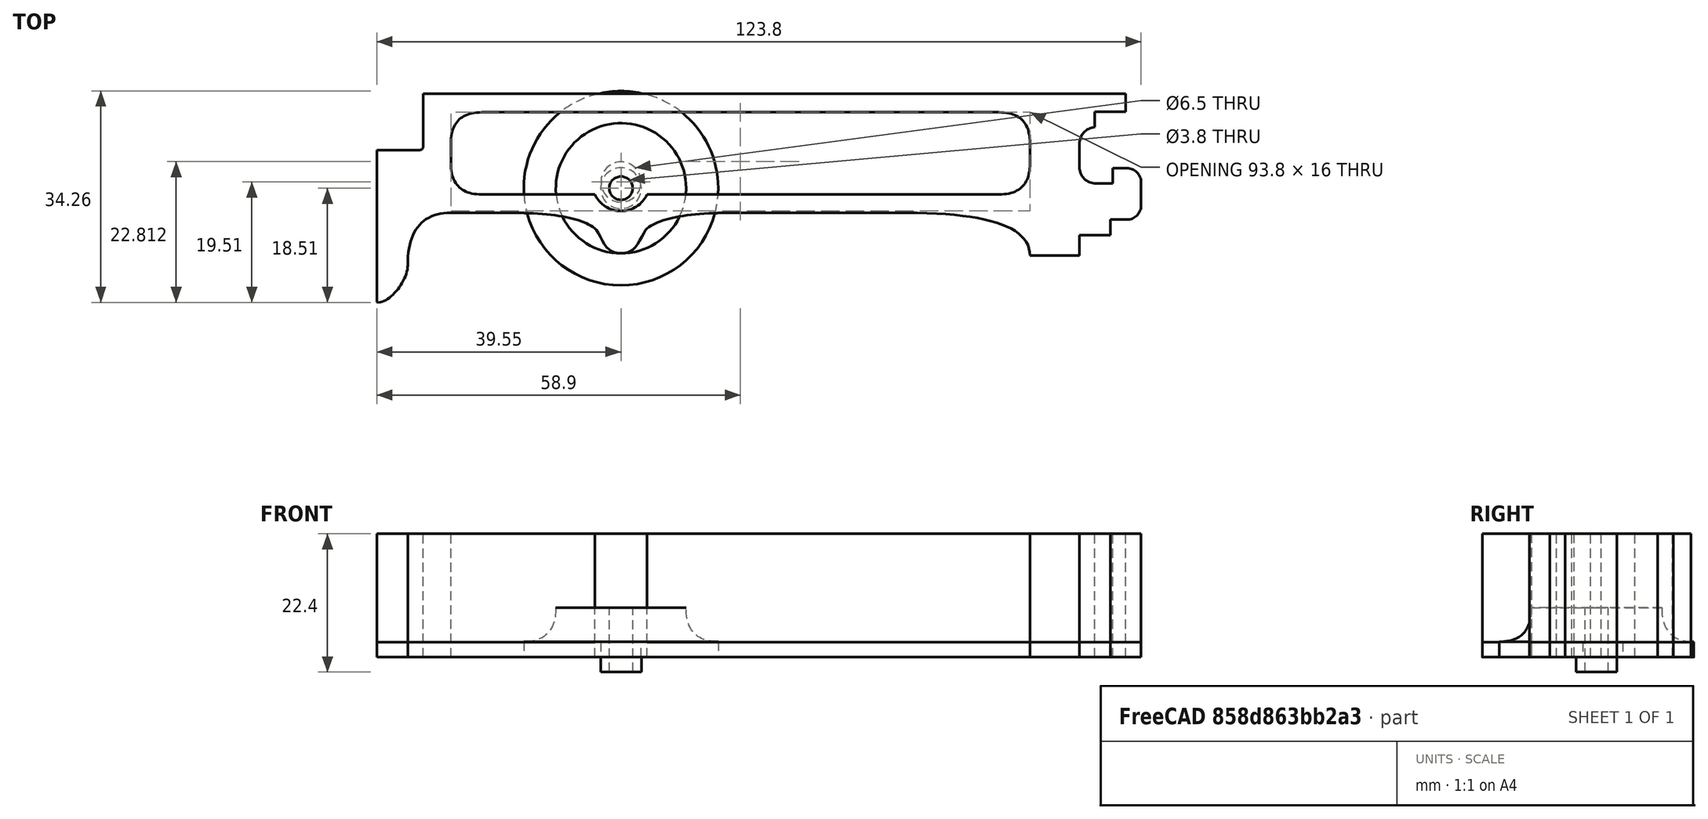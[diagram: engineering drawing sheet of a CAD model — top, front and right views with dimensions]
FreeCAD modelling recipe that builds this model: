
FCSTD DOCUMENT  (FreeCAD 0.19R0.19.2)
Label: v0_16
License: All rights reserved
LicenseURL: http://en.wikipedia.org/wiki/All_rights_reserved
objects: Sketcher::SketchObject×3, Part::Extrusion×2, Part::Revolution×1
note: 6 computed .brp shape members not serialized (recipe doc carries the construction recipe); baked Part::Feature solids carry a one-line shape summary decoded from their .brp

FEATURE [Sketcher::SketchObject] Sketch
  FullyConstrained = true
  sketch-geometry (69):
    g0: ArcOfCircle CenterX=-20 CenterY=-14.35 CenterZ=0 NormalX=0 NormalY=0 NormalZ=1 AngleXU=0 Radius=2.3 StartAngle=8e-16 EndAngle=1.5708
    g1: ArcOfCircle CenterX=-20 CenterY=-18.1 CenterZ=0 NormalX=0 NormalY=0 NormalZ=1 AngleXU=0 Radius=2.3 StartAngle=4.71239 EndAngle=6.28319
    g2: LineSegment StartX=-20 StartY=-20.4 StartZ=0 EndX=-22.7 EndY=-20.4 EndZ=0
    g3: LineSegment StartX=-22.7 StartY=-22.9 StartZ=0 EndX=-22.7 EndY=-20.4 EndZ=0
    g4: LineSegment StartX=-17.7 StartY=-14.35 StartZ=0 EndX=-17.7 EndY=-18.1 EndZ=0
    g5: LineSegment StartX=-25.2 StartY=-5.40742 StartZ=0 EndX=-25.2 EndY=-2.9 EndZ=0
    g6: LineSegment StartX=-25.2 StartY=-2.9 StartZ=0 EndX=-20.2 EndY=-2.9 EndZ=0
    g7: LineSegment StartX=-20.2 StartY=-2.9 StartZ=0 EndX=-20.2 EndY=0 EndZ=0
    g8: ArcOfCircle CenterX=-25 CenterY=-8.1 CenterZ=0 NormalX=0 NormalY=0 NormalZ=1 AngleXU=0 Radius=2.7 StartAngle=1.64494 EndAngle=3.14159
    g9: ArcOfCircle CenterX=-25 CenterY=-11.85 CenterZ=0 NormalX=0 NormalY=0 NormalZ=1 AngleXU=0 Radius=2.7 StartAngle=3.14159 EndAngle=4.71239
    g10: LineSegment StartX=-27.7 StartY=-8.1 StartZ=0 EndX=-27.7 EndY=-11.85 EndZ=0
    g11: LineSegment StartX=-25 StartY=-14.55 StartZ=0 EndX=-22.3 EndY=-14.55 EndZ=0
    g12: LineSegment StartX=-22.3 StartY=-12.05 StartZ=0 EndX=-22.3 EndY=-14.55 EndZ=0
    g13: LineSegment StartX=-22.3 StartY=-12.05 StartZ=0 EndX=-20 EndY=-12.05 EndZ=0
    g14: LineSegment StartX=-27.7 StartY=-22.9 StartZ=0 EndX=-22.7 EndY=-22.9 EndZ=0
    g15: LineSegment StartX=-27.7 StartY=-22.9 StartZ=0 EndX=-27.7 EndY=-26.2 EndZ=0
    g16: Circle CenterX=-101.95 CenterY=-14.3 CenterZ=0 NormalX=0 NormalY=0 NormalZ=1 AngleXU=0 Radius=3.25
    g17: LineSegment StartX=-134 StartY=0 StartZ=0 EndX=-20.2 EndY=0 EndZ=0
    g18: LineSegment StartX=-134 StartY=2.68e-14 StartZ=0 EndX=-134 EndY=-8.6 EndZ=0
    g19: LineSegment StartX=-134.5 StartY=-9.1 StartZ=0 EndX=-141.5 EndY=-9.1 EndZ=0
    g20: ArcOfCircle CenterX=-134.5 CenterY=-8.6 CenterZ=0 NormalX=0 NormalY=0 NormalZ=1 AngleXU=0 Radius=0.5 StartAngle=4.71239 EndAngle=6.28319
    g21: Circle CenterX=-97.7 CenterY=-21.8 CenterZ=0 NormalX=0 NormalY=0 NormalZ=1 AngleXU=0 Radius=1
    g22: Circle CenterX=-94.45 CenterY=-19.3 CenterZ=0 NormalX=0 NormalY=0 NormalZ=1 AngleXU=0 Radius=1
    g23: Circle CenterX=-84.45 CenterY=-19.3 CenterZ=0 NormalX=0 NormalY=0 NormalZ=1 AngleXU=0 Radius=1
    g24: BSplineCurve PolesCount=3 KnotsCount=2 Degree=2 IsPeriodic=0
    g25: GeomPoint X=-97.7 Y=-21.8 Z=0
    g26: GeomPoint X=-84.45 Y=-19.3 Z=0
    g27: Circle CenterX=-106.2 CenterY=-21.8 CenterZ=0 NormalX=0 NormalY=0 NormalZ=1 AngleXU=0 Radius=1
    g28: Circle CenterX=-109.45 CenterY=-19.3 CenterZ=0 NormalX=0 NormalY=0 NormalZ=1 AngleXU=0 Radius=1
    g29: Circle CenterX=-119.45 CenterY=-19.3 CenterZ=0 NormalX=0 NormalY=0 NormalZ=1 AngleXU=0 Radius=1
    g30: BSplineCurve PolesCount=3 KnotsCount=2 Degree=2 IsPeriodic=0
    g31: GeomPoint X=-106.2 Y=-21.8 Z=0
    g32: GeomPoint X=-119.45 Y=-19.3 Z=0
    g33: LineSegment StartX=-141.5 StartY=-9.1 StartZ=0 EndX=-141.5 EndY=-33.8 EndZ=0
    g34-g37: Circle x4 (B-spline internal-alignment scaffolding for g38; pole/knot coordinates omitted)
    g38: BSplineCurve PolesCount=4 KnotsCount=2 Degree=3 IsPeriodic=0
    g39: GeomPoint X=-141.5 Y=-33.8 Z=0
    g40: GeomPoint X=-136.5 Y=-27.8 Z=0
    g41: Circle CenterX=-136.5 CenterY=-27.8 CenterZ=0 NormalX=0 NormalY=0 NormalZ=1 AngleXU=0 Radius=1
    g42: Circle CenterX=-136.5 CenterY=-19.3 CenterZ=0 NormalX=0 NormalY=0 NormalZ=1 AngleXU=0 Radius=1
    g43: Circle CenterX=-129.5 CenterY=-19.3 CenterZ=0 NormalX=0 NormalY=0 NormalZ=1 AngleXU=0 Radius=1
    g44: BSplineCurve PolesCount=3 KnotsCount=2 Degree=2 IsPeriodic=0
    g45: GeomPoint X=-136.5 Y=-27.8 Z=0
    g46: GeomPoint X=-129.5 Y=-19.3 Z=0
    g47: LineSegment StartX=-129.5 StartY=-19.3 StartZ=0 EndX=-119.45 EndY=-19.3 EndZ=0
    g48: LineSegment StartX=-35.7 StartY=-26.2 StartZ=0 EndX=-27.7 EndY=-26.2 EndZ=0
    g49: Circle CenterX=-35.7 CenterY=-26.2 CenterZ=0 NormalX=0 NormalY=0 NormalZ=1 AngleXU=0 Radius=1
    g50: Circle CenterX=-35.7 CenterY=-19.3 CenterZ=0 NormalX=0 NormalY=0 NormalZ=1 AngleXU=0 Radius=1
    g51: Circle CenterX=-55.7 CenterY=-19.3 CenterZ=0 NormalX=0 NormalY=0 NormalZ=1 AngleXU=0 Radius=1
    g52: BSplineCurve PolesCount=3 KnotsCount=2 Degree=2 IsPeriodic=0
    g53: GeomPoint X=-35.7 Y=-26.2 Z=0
    g54: GeomPoint X=-55.7 Y=-19.3 Z=0
    g55: LineSegment StartX=-84.45 StartY=-19.3 StartZ=0 EndX=-55.7 EndY=-19.3 EndZ=0
    g56-g62: Circle x7 (B-spline internal-alignment scaffolding for g63; pole/knot coordinates omitted)
    g63: BSplineCurve PolesCount=7 KnotsCount=5 Degree=3 IsPeriodic=0
    g64-g68: GeomPoint x5 (B-spline internal-alignment scaffolding for g63; pole/knot coordinates omitted)
  constraints (111):
    c: Block(g1)
    c: Block(g0)
    c: Coincident(g2,g1)
    c: Horizontal(g2)
    c: Vertical(g3)
    c: Coincident(g3,g2)
    c: Coincident(g4,g0)
    c: Coincident(g4,g1)
    c: Vertical(g4)
    c: Vertical(g5)
    c: Block(g5)
    c: Coincident(g6,g5)
    c: Horizontal(g6)
    c: Vertical(g7)
    c: Block(g7)
    c: Block(g6)
    c: Coincident(g8,g5)
    c: Block(g9)
    c: Coincident(g10,g8)
    c: Coincident(g10,g9)
    c: Vertical(g10)
    c: Block(g10)
    c: Coincident(g11,g9)
    c: Horizontal(g11)
    c: Vertical(g12)
    c: Coincident(g12,g11)
    c: Block(g12)
    c: Coincident(g13,g0)
    c: Horizontal(g13)
    c: Block(g13)
    c: Coincident(g14,g3)
    c: Horizontal(g14)
    c: Block(g14)
    c: Coincident(g15,g14)
    c: Vertical(g15)
    c: Block(g16)
    c: Coincident(g17,g7)
    c: Horizontal(g17)
    c: Vertical(g18)
    c: Distance(g18) = 8.6
    c: Horizontal(g19)
    c: Distance(g19) = 7
    c: Coincident(g20,g18)
    c: Coincident(g20,g19)
    c: Block(g20)
    c: Block(g17)
    c: Weight(g21) = 1
    c: Equal(g21,g22)
    c: Equal(g21,g23)
    c: InternalAlignment(g21,g24)
    c: InternalAlignment(g22,g24)
    c: InternalAlignment(g23,g24)
    c: InternalAlignment(g25,g24)
    c: InternalAlignment(g26,g24)
    c: Weight(g27) = 1
    c: Equal(g27,g28)
    c: Equal(g27,g29)
    c: InternalAlignment(g27,g30)
    c: InternalAlignment(g28,g30)
    c: InternalAlignment(g29,g30)
    c: InternalAlignment(g31,g30)
    c: InternalAlignment(g32,g30)
    c: Block(g30)
    c: Block(g24)
    c: Coincident(g33,g19)
    c: Vertical(g33)
    c: Block(g33)
    c: Coincident(g38,g33)
    c: Weight(g34) = 1
    c: Equal(g34,g35)
    c: Equal(g34,g36)
    c: Equal(g34,g37)
    c: InternalAlignment(g34-g37 -> g38) x4
    c: InternalAlignment(g39,g38)
    c: InternalAlignment(g40,g38)
    c: Weight(g41) = 1
    c: Equal(g41,g42)
    c: Equal(g41,g43)
    c: InternalAlignment(g41,g44)
    c: InternalAlignment(g42,g44)
    c: InternalAlignment(g43,g44)
    c: InternalAlignment(g45,g44)
    c: InternalAlignment(g46,g44)
    c: Block(g38)
    c: Block(g44)
    c: Coincident(g47,g44)
    c: Coincident(g47,g30)
    c: Horizontal(g47)
    c: Horizontal(g48)
    c: Distance(g48) = 8
    c: Block(g48)
    c: Block(g15)
    c: Block(g8)
    c: Coincident(g52,g48)
    c: Weight(g49) = 1
    c: Equal(g49,g50)
    c: Equal(g49,g51)
    c: InternalAlignment(g49,g52)
    c: InternalAlignment(g50,g52)
    c: InternalAlignment(g51,g52)
    c: InternalAlignment(g53,g52)
    c: InternalAlignment(g54,g52)
    c: Block(g52)
    c: Coincident(g55,g24)
    c: Coincident(g55,g52)
    c: Horizontal(g55)
    c: Weight(g56) = 1
    c: Equal(g56, g57-g62) x6
    c: InternalAlignment(g56-g62 -> g63) x7
    c: InternalAlignment(g64-g68 -> g63) x5
    c: Block(g63)
FEATURE [Part::Extrusion] Extrude
  Base = -> Sketch
  Dir = (0,0,1)
  DirMode = 2
  FaceMakerClass = Part::FaceMakerBullseye
  LengthFwd = 2.4
  LengthRev = 0
  Solid = true
  Symmetric = false
FEATURE [Sketcher::SketchObject] Sketch001
  FullyConstrained = true
  sketch-geometry (98):
    g0: ArcOfCircle CenterX=-20 CenterY=-14.35 CenterZ=0 NormalX=0 NormalY=0 NormalZ=1 AngleXU=0 Radius=2.3 StartAngle=8e-16 EndAngle=1.5708
    g1: ArcOfCircle CenterX=-20 CenterY=-18.1 CenterZ=0 NormalX=0 NormalY=0 NormalZ=1 AngleXU=0 Radius=2.3 StartAngle=4.71239 EndAngle=6.28319
    g2: LineSegment StartX=-20 StartY=-20.4 StartZ=0 EndX=-22.7 EndY=-20.4 EndZ=0
    g3: LineSegment StartX=-22.7 StartY=-22.9 StartZ=0 EndX=-22.7 EndY=-20.4 EndZ=0
    g4: LineSegment StartX=-17.7 StartY=-14.35 StartZ=0 EndX=-17.7 EndY=-18.1 EndZ=0
    g5: LineSegment StartX=-25.2 StartY=-5.40742 StartZ=0 EndX=-25.2 EndY=-2.9 EndZ=0
    g6: LineSegment StartX=-25.2 StartY=-2.9 StartZ=0 EndX=-20.2 EndY=-2.9 EndZ=0
    g7: LineSegment StartX=-20.2 StartY=-2.9 StartZ=0 EndX=-20.2 EndY=0 EndZ=0
    g8: ArcOfCircle CenterX=-25 CenterY=-8.1 CenterZ=0 NormalX=0 NormalY=0 NormalZ=1 AngleXU=0 Radius=2.7 StartAngle=1.64494 EndAngle=3.14159
    g9: ArcOfCircle CenterX=-25 CenterY=-11.85 CenterZ=0 NormalX=0 NormalY=0 NormalZ=1 AngleXU=0 Radius=2.7 StartAngle=3.14159 EndAngle=4.71239
    g10: LineSegment StartX=-27.7 StartY=-8.1 StartZ=0 EndX=-27.7 EndY=-11.85 EndZ=0
    g11: LineSegment StartX=-25 StartY=-14.55 StartZ=0 EndX=-22.3 EndY=-14.55 EndZ=0
    g12: LineSegment StartX=-22.3 StartY=-12.05 StartZ=0 EndX=-22.3 EndY=-14.55 EndZ=0
    g13: LineSegment StartX=-22.3 StartY=-12.05 StartZ=0 EndX=-20 EndY=-12.05 EndZ=0
    g14: LineSegment StartX=-27.7 StartY=-22.9 StartZ=0 EndX=-22.7 EndY=-22.9 EndZ=0
    g15: LineSegment StartX=-27.7 StartY=-22.9 StartZ=0 EndX=-27.7 EndY=-26.2 EndZ=0
    g16: LineSegment StartX=-134 StartY=0 StartZ=0 EndX=-134 EndY=-8.6 EndZ=0
    g17: LineSegment StartX=-134.5 StartY=-9.1 StartZ=0 EndX=-141.5 EndY=-9.1 EndZ=0
    g18: ArcOfCircle CenterX=-134.5 CenterY=-8.6 CenterZ=0 NormalX=0 NormalY=0 NormalZ=1 AngleXU=0 Radius=0.5 StartAngle=4.71239 EndAngle=6.28319
    g19: Circle CenterX=-97.7 CenterY=-21.8 CenterZ=0 NormalX=0 NormalY=0 NormalZ=1 AngleXU=0 Radius=1
    g20: Circle CenterX=-94.45 CenterY=-19.3 CenterZ=0 NormalX=0 NormalY=0 NormalZ=1 AngleXU=0 Radius=1
    g21: Circle CenterX=-84.45 CenterY=-19.3 CenterZ=0 NormalX=0 NormalY=0 NormalZ=1 AngleXU=0 Radius=1
    g22: BSplineCurve PolesCount=3 KnotsCount=2 Degree=2 IsPeriodic=0
    g23: GeomPoint X=-97.7 Y=-21.8 Z=0
    g24: GeomPoint X=-84.45 Y=-19.3 Z=0
    g25: Circle CenterX=-106.2 CenterY=-21.8 CenterZ=0 NormalX=0 NormalY=0 NormalZ=1 AngleXU=0 Radius=1
    g26: Circle CenterX=-109.45 CenterY=-19.3 CenterZ=0 NormalX=0 NormalY=0 NormalZ=1 AngleXU=0 Radius=1
    g27: Circle CenterX=-119.45 CenterY=-19.3 CenterZ=0 NormalX=0 NormalY=0 NormalZ=1 AngleXU=0 Radius=1
    g28: BSplineCurve PolesCount=3 KnotsCount=2 Degree=2 IsPeriodic=0
    g29: GeomPoint X=-106.2 Y=-21.8 Z=0
    g30: GeomPoint X=-119.45 Y=-19.3 Z=0
    g31: LineSegment StartX=-141.5 StartY=-9.1 StartZ=0 EndX=-141.5 EndY=-33.8 EndZ=0
    g32-g35: Circle x4 (B-spline internal-alignment scaffolding for g36; pole/knot coordinates omitted)
    g36: BSplineCurve PolesCount=4 KnotsCount=2 Degree=3 IsPeriodic=0
    g37: GeomPoint X=-141.5 Y=-33.8 Z=0
    g38: GeomPoint X=-136.5 Y=-27.8 Z=0
    g39: Circle CenterX=-136.5 CenterY=-27.8 CenterZ=0 NormalX=0 NormalY=0 NormalZ=1 AngleXU=0 Radius=1
    g40: Circle CenterX=-136.5 CenterY=-19.3 CenterZ=0 NormalX=0 NormalY=0 NormalZ=1 AngleXU=0 Radius=1
    g41: Circle CenterX=-129.5 CenterY=-19.3 CenterZ=0 NormalX=0 NormalY=0 NormalZ=1 AngleXU=0 Radius=1
    g42: BSplineCurve PolesCount=3 KnotsCount=2 Degree=2 IsPeriodic=0
    g43: GeomPoint X=-136.5 Y=-27.8 Z=0
    g44: GeomPoint X=-129.5 Y=-19.3 Z=0
    g45: LineSegment StartX=-129.5 StartY=-19.3 StartZ=0 EndX=-119.45 EndY=-19.3 EndZ=0
    g46: LineSegment StartX=-35.7 StartY=-26.2 StartZ=0 EndX=-27.7 EndY=-26.2 EndZ=0
    g47: Circle CenterX=-35.7 CenterY=-26.2 CenterZ=0 NormalX=0 NormalY=0 NormalZ=1 AngleXU=0 Radius=1
    g48: Circle CenterX=-35.7 CenterY=-19.3 CenterZ=0 NormalX=0 NormalY=0 NormalZ=1 AngleXU=0 Radius=1
    g49: Circle CenterX=-55.7 CenterY=-19.3 CenterZ=0 NormalX=0 NormalY=0 NormalZ=1 AngleXU=0 Radius=1
    g50: BSplineCurve PolesCount=3 KnotsCount=2 Degree=2 IsPeriodic=0
    g51: GeomPoint X=-35.7 Y=-26.2 Z=0
    g52: GeomPoint X=-55.7 Y=-19.3 Z=0
    g53: LineSegment StartX=-84.45 StartY=-19.3 StartZ=0 EndX=-55.7 EndY=-19.3 EndZ=0
    g54-g60: Circle x7 (B-spline internal-alignment scaffolding for g61; pole/knot coordinates omitted)
    g61: BSplineCurve PolesCount=7 KnotsCount=5 Degree=3 IsPeriodic=0
    g62-g66: GeomPoint x5 (B-spline internal-alignment scaffolding for g61; pole/knot coordinates omitted)
    g67: LineSegment StartX=-134 StartY=0 StartZ=0 EndX=-20.2 EndY=0 EndZ=0
    g68: ArcOfCircle CenterX=-101.95 CenterY=-14.3 CenterZ=0 NormalX=0 NormalY=0 NormalZ=1 AngleXU=0 Radius=4.69707 StartAngle=3.58144 EndAngle=5.84334
    g69: Circle CenterX=-40.7 CenterY=-3 CenterZ=0 NormalX=0 NormalY=0 NormalZ=1 AngleXU=0 Radius=1
    g70: Circle CenterX=-35.7 CenterY=-3 CenterZ=0 NormalX=0 NormalY=0 NormalZ=1 AngleXU=0 Radius=1
    g71: Circle CenterX=-35.7 CenterY=-8 CenterZ=0 NormalX=0 NormalY=0 NormalZ=1 AngleXU=0 Radius=1
    g72: BSplineCurve PolesCount=3 KnotsCount=2 Degree=2 IsPeriodic=0
    g73: GeomPoint X=-40.7 Y=-3 Z=0
    g74: GeomPoint X=-35.7 Y=-8 Z=0
    g75: Circle CenterX=-35.7 CenterY=-11.3 CenterZ=0 NormalX=0 NormalY=0 NormalZ=1 AngleXU=0 Radius=1
    g76: Circle CenterX=-35.7 CenterY=-16.3 CenterZ=0 NormalX=0 NormalY=0 NormalZ=1 AngleXU=0 Radius=1
    g77: Circle CenterX=-40.7 CenterY=-16.3 CenterZ=0 NormalX=0 NormalY=0 NormalZ=1 AngleXU=0 Radius=1
    g78: BSplineCurve PolesCount=3 KnotsCount=2 Degree=2 IsPeriodic=0
    g79: GeomPoint X=-35.7 Y=-11.3 Z=0
    g80: GeomPoint X=-40.7 Y=-16.3 Z=0
    g81: Circle CenterX=-124.5 CenterY=-16.3 CenterZ=0 NormalX=0 NormalY=0 NormalZ=1 AngleXU=0 Radius=1
    g82: Circle CenterX=-129.5 CenterY=-16.3 CenterZ=0 NormalX=0 NormalY=0 NormalZ=1 AngleXU=0 Radius=1
    g83: Circle CenterX=-129.5 CenterY=-11.3 CenterZ=0 NormalX=0 NormalY=0 NormalZ=1 AngleXU=0 Radius=1
    g84: BSplineCurve PolesCount=3 KnotsCount=2 Degree=2 IsPeriodic=0
    g85: GeomPoint X=-124.5 Y=-16.3 Z=0
    g86: GeomPoint X=-129.5 Y=-11.3 Z=0
    g87: Circle CenterX=-129.5 CenterY=-8 CenterZ=0 NormalX=0 NormalY=0 NormalZ=1 AngleXU=0 Radius=1
    g88: Circle CenterX=-129.5 CenterY=-3 CenterZ=0 NormalX=0 NormalY=0 NormalZ=1 AngleXU=0 Radius=1
    g89: Circle CenterX=-124.5 CenterY=-3 CenterZ=0 NormalX=0 NormalY=0 NormalZ=1 AngleXU=0 Radius=1
    g90: BSplineCurve PolesCount=3 KnotsCount=2 Degree=2 IsPeriodic=0
    g91: GeomPoint X=-129.5 Y=-8 Z=0
    g92: GeomPoint X=-124.5 Y=-3 Z=0
    g93: LineSegment StartX=-129.5 StartY=-8 StartZ=0 EndX=-129.5 EndY=-11.3 EndZ=0
    g94: LineSegment StartX=-124.5 StartY=-3 StartZ=0 EndX=-40.7 EndY=-3 EndZ=0
    g95: LineSegment StartX=-35.7 StartY=-8 StartZ=0 EndX=-35.7 EndY=-11.3 EndZ=0
    g96: LineSegment StartX=-40.7 StartY=-16.3 StartZ=0 EndX=-97.7 EndY=-16.3 EndZ=0
    g97: LineSegment StartX=-106.2 StartY=-16.3 StartZ=0 EndX=-124.5 EndY=-16.3 EndZ=0
  constraints (162):
    c: Block(g1)
    c: Block(g0)
    c: Coincident(g2,g1)
    c: Horizontal(g2)
    c: Vertical(g3)
    c: Coincident(g3,g2)
    c: Coincident(g4,g0)
    c: Coincident(g4,g1)
    c: Vertical(g4)
    c: Vertical(g5)
    c: Block(g5)
    c: Coincident(g6,g5)
    c: Horizontal(g6)
    c: Vertical(g7)
    c: Block(g7)
    c: Block(g6)
    c: Coincident(g8,g5)
    c: Block(g9)
    c: Coincident(g10,g8)
    c: Coincident(g10,g9)
    c: Vertical(g10)
    c: Block(g10)
    c: Coincident(g11,g9)
    c: Horizontal(g11)
    c: Vertical(g12)
    c: Coincident(g12,g11)
    c: Block(g12)
    c: Coincident(g13,g0)
    c: Horizontal(g13)
    c: Block(g13)
    c: Coincident(g14,g3)
    c: Horizontal(g14)
    c: Block(g14)
    c: Coincident(g15,g14)
    c: Vertical(g15)
    c: Vertical(g16)
    c: Distance(g16) = 8.6
    c: Horizontal(g17)
    c: Distance(g17) = 7
    c: Coincident(g18,g16)
    c: Coincident(g18,g17)
    c: Block(g18)
    c: Weight(g19) = 1
    c: Equal(g19,g20)
    c: Equal(g19,g21)
    c: InternalAlignment(g19,g22)
    c: InternalAlignment(g20,g22)
    c: InternalAlignment(g21,g22)
    c: InternalAlignment(g23,g22)
    c: InternalAlignment(g24,g22)
    c: Weight(g25) = 1
    c: Equal(g25,g26)
    c: Equal(g25,g27)
    c: InternalAlignment(g25,g28)
    c: InternalAlignment(g26,g28)
    c: InternalAlignment(g27,g28)
    c: InternalAlignment(g29,g28)
    c: InternalAlignment(g30,g28)
    c: Block(g22)
    c: Coincident(g31,g17)
    c: Vertical(g31)
    c: Block(g31)
    c: Coincident(g36,g31)
    c: Weight(g32) = 1
    c: Equal(g32,g33)
    c: Equal(g32,g34)
    c: Equal(g32,g35)
    c: InternalAlignment(g32-g35 -> g36) x4
    c: InternalAlignment(g37,g36)
    c: InternalAlignment(g38,g36)
    c: Weight(g39) = 1
    c: Equal(g39,g40)
    c: Equal(g39,g41)
    c: InternalAlignment(g39,g42)
    c: InternalAlignment(g40,g42)
    c: InternalAlignment(g41,g42)
    c: InternalAlignment(g43,g42)
    c: InternalAlignment(g44,g42)
    c: Block(g36)
    c: Coincident(g45,g42)
    c: Coincident(g45,g28)
    c: Horizontal(g45)
    c: Horizontal(g46)
    c: Distance(g46) = 8
    c: Block(g46)
    c: Block(g15)
    c: Block(g8)
    c: Coincident(g50,g46)
    c: Weight(g47) = 1
    c: Equal(g47,g48)
    c: Equal(g47,g49)
    c: InternalAlignment(g47,g50)
    c: InternalAlignment(g48,g50)
    c: InternalAlignment(g49,g50)
    c: InternalAlignment(g51,g50)
    c: InternalAlignment(g52,g50)
    c: Block(g50)
    c: Coincident(g53,g22)
    c: Coincident(g53,g50)
    c: Horizontal(g53)
    c: Weight(g54) = 1
    c: Equal(g54, g55-g60) x6
    c: InternalAlignment(g54-g60 -> g61) x7
    c: InternalAlignment(g62-g66 -> g61) x5
    c: Block(g61)
    c: Coincident(g67,g16)
    c: Coincident(g67,g7)
    c: Horizontal(g67)
    c: Block(g68)
    c: Block(g28)
    c: Block(g42)
    c: Weight(g69) = 1
    c: Equal(g69,g70)
    c: Equal(g69,g71)
    c: InternalAlignment(g69,g72)
    c: InternalAlignment(g70,g72)
    c: InternalAlignment(g71,g72)
    c: InternalAlignment(g73,g72)
    c: InternalAlignment(g74,g72)
    c: Weight(g75) = 1
    c: Equal(g75,g76)
    c: Equal(g75,g77)
    c: InternalAlignment(g75,g78)
    c: InternalAlignment(g76,g78)
    c: InternalAlignment(g77,g78)
    c: InternalAlignment(g79,g78)
    c: InternalAlignment(g80,g78)
    c: Weight(g81) = 1
    c: Equal(g81,g82)
    c: Equal(g81,g83)
    c: InternalAlignment(g81,g84)
    c: InternalAlignment(g82,g84)
    c: InternalAlignment(g83,g84)
    c: InternalAlignment(g85,g84)
    c: InternalAlignment(g86,g84)
    c: Weight(g87) = 1
    c: Equal(g87,g88)
    c: Equal(g87,g89)
    c: InternalAlignment(g87,g90)
    c: InternalAlignment(g88,g90)
    c: InternalAlignment(g89,g90)
    c: InternalAlignment(g91,g90)
    c: InternalAlignment(g92,g90)
    c: Block(g90)
    c: Block(g84)
    c: Block(g78)
    c: Block(g72)
    c: Coincident(g93,g90)
    c: Coincident(g93,g84)
    c: Vertical(g93)
    c: Coincident(g94,g90)
    c: Horizontal(g94)
    c: Coincident(g95,g72)
    c: Coincident(g95,g78)
    c: Vertical(g95)
    c: Coincident(g96,g78)
    c: Coincident(g96,g68)
    c: Horizontal(g96)
    c: Coincident(g97,g68)
    c: Coincident(g97,g84)
    c: Horizontal(g97)
    c: Block(g94)
FEATURE [Part::Extrusion] Extrude001
  Base = -> Sketch001
  Dir = (0,0,1)
  DirMode = 2
  FaceMakerClass = Part::FaceMakerBullseye
  LengthFwd = 20
  LengthRev = 0
  Solid = true
  Symmetric = false
FEATURE [Sketcher::SketchObject] Sketch004
  FullyConstrained = true
  Placement = pos=(0,0,0) rot=(1,0,0;1.5708rad)
  sketch-geometry (12):
    g0: LineSegment StartX=15.75 StartY=2.5 StartZ=0 EndX=15.75 EndY=0 EndZ=0
    g1: Circle CenterX=15.75 CenterY=2.5 CenterZ=0 NormalX=0 NormalY=0 NormalZ=1 AngleXU=0 Radius=1
    g2: Circle CenterX=10.55 CenterY=2.5 CenterZ=0 NormalX=0 NormalY=0 NormalZ=1 AngleXU=0 Radius=1
    g3: Circle CenterX=10.55 CenterY=8 CenterZ=0 NormalX=0 NormalY=0 NormalZ=1 AngleXU=0 Radius=1
    g4: BSplineCurve PolesCount=3 KnotsCount=2 Degree=2 IsPeriodic=0
    g5: GeomPoint X=15.75 Y=2.5 Z=0
    g6: GeomPoint X=10.55 Y=8 Z=0
    g7: LineSegment StartX=1.9 StartY=8 StartZ=0 EndX=10.55 EndY=8 EndZ=0
    g8: LineSegment StartX=1.9 StartY=-2.4 StartZ=0 EndX=1.9 EndY=8 EndZ=0
    g9: LineSegment StartX=3.30092 StartY=-2.4 StartZ=0 EndX=3.30092 EndY=0 EndZ=0
    g10: LineSegment StartX=15.75 StartY=0 StartZ=0 EndX=3.30092 EndY=0 EndZ=0
    g11: LineSegment StartX=3.30092 StartY=-2.4 StartZ=0 EndX=1.9 EndY=-2.4 EndZ=0
  constraints (26):
    c: Vertical(g0)
    c: Distance(g0) = 2.5
    c: Coincident(g4,g0)
    c: Weight(g1) = 1
    c: Equal(g1,g2)
    c: Equal(g1,g3)
    c: InternalAlignment(g1,g4)
    c: InternalAlignment(g2,g4)
    c: InternalAlignment(g3,g4)
    c: InternalAlignment(g5,g4)
    c: InternalAlignment(g6,g4)
    c: Block(g4)
    c: Coincident(g7,g4)
    c: Horizontal(g7)
    c: Vertical(g8)
    c: Coincident(g8,g7)
    c: Block(g8)
    c: Vertical(g9)
    c: Coincident(g10,g0)
    c: PointOnObject(g10,g-1)
    c: Horizontal(g10)
    c: Coincident(g10,g9)
    c: Block(g9)
    c: Coincident(g11,g9)
    c: Coincident(g11,g8)
    c: Horizontal(g11)
FEATURE [Part::Revolution] Revolve  label="mainScrewStandRevolve"
  Angle = 360
  Axis = (0,0,1)
  Base = (0,0,0)
  FaceMakerClass = Part::FaceMakerBullseye
  Placement = pos=(-101.95,-15.3,0) rot=(0,0,1;0rad)
  Solid = true
  Source = -> Sketch004
  Symmetric = false
